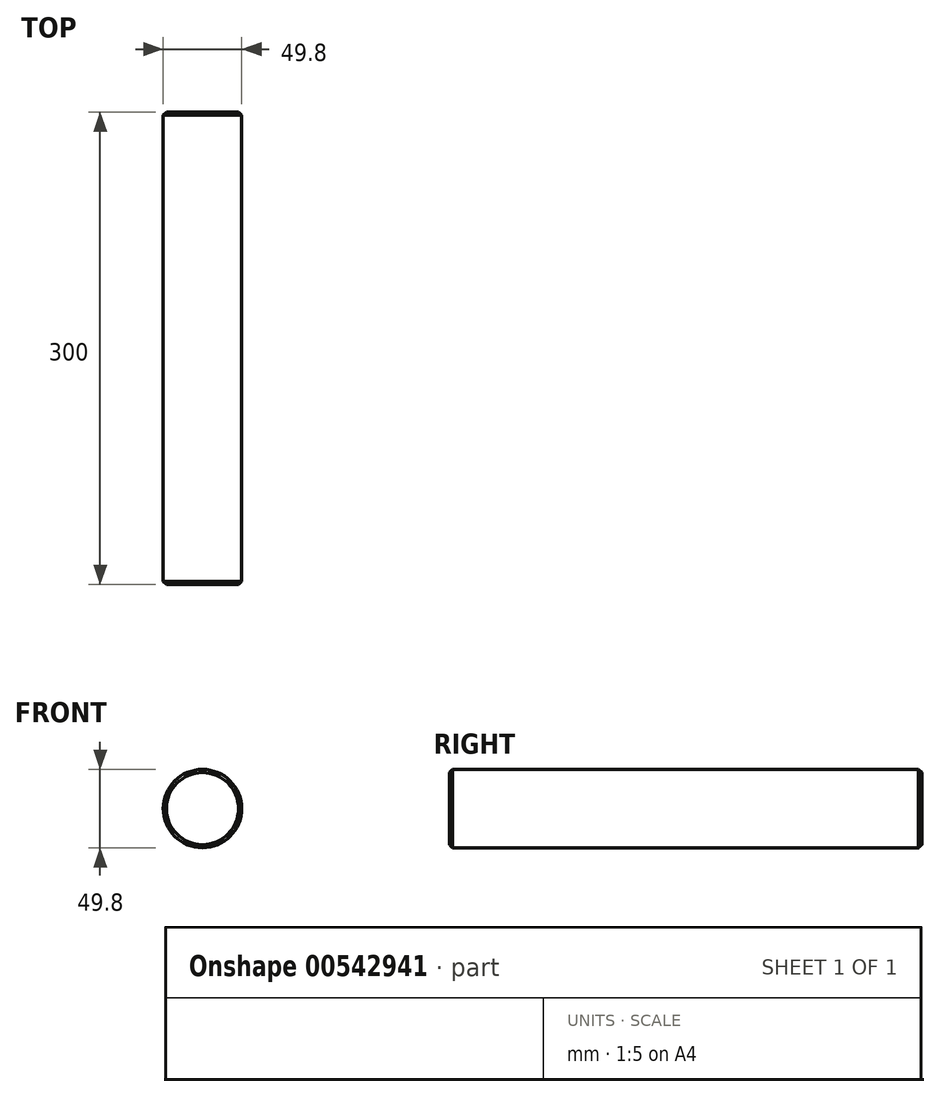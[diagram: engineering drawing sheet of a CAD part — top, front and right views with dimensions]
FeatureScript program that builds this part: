
annotation { "Feature Type Name" : "Feature", "Feature Type Description" : "" }
export const myFeature = defineFeature(function(context is Context, id is Id, definition is map)
    precondition{}
    {
        {
            var Q0;
            Q0=qCreatedBy(makeId("Front.planeOp"),FACE);
            var sketch = newSketch(context, id + "F0", { "sketchPlane" : qUnion([Q0])});
            skCircle(sketch, "E0", {"center": v(0, 0) * mm, "radius": 24.9 * mm});
            skSolve(sketch);
        }
        {
            var Q0;
            Q0=makeQuery(id+"F0.imprint","IMPRINT",FACE,{"disambiguationData":[TD([[makeQuery(id+"F0.imprint","IMPRINT",EDGE,{"derivedFrom":sQuery(id+"F0.wireOp",EDGE,"E0")}),1.0]])]});
            extrude(context, id + "F1", {"entities" : qUnion([Q0]), "depth" : 300 * mm, "offsetDistance" : 25.4 * mm});
        }
        {
            var Q0;
            Q0=makeQuery(id+"F1.opExtrude","CAP_EDGE",EDGE,{"disambiguationData":[OSD([sQuery(id+"F0.wireOp",EDGE,"E0")])],"isStart":false});
            chamfer(context, id + "F2", {"entities" : qUnion([Q0]), "width" : 2 * mm, "tangentPropagation" : true});
        }
        {
            var Q0;
            Q0=makeQuery(id+"F1.opExtrude","CAP_EDGE",EDGE,{"disambiguationData":[OSD([sQuery(id+"F0.wireOp",EDGE,"E0")])],"isStart":true});
            chamfer(context, id + "F3", {"entities" : qUnion([Q0]), "width" : 2 * mm, "tangentPropagation" : true});
        }
    });
